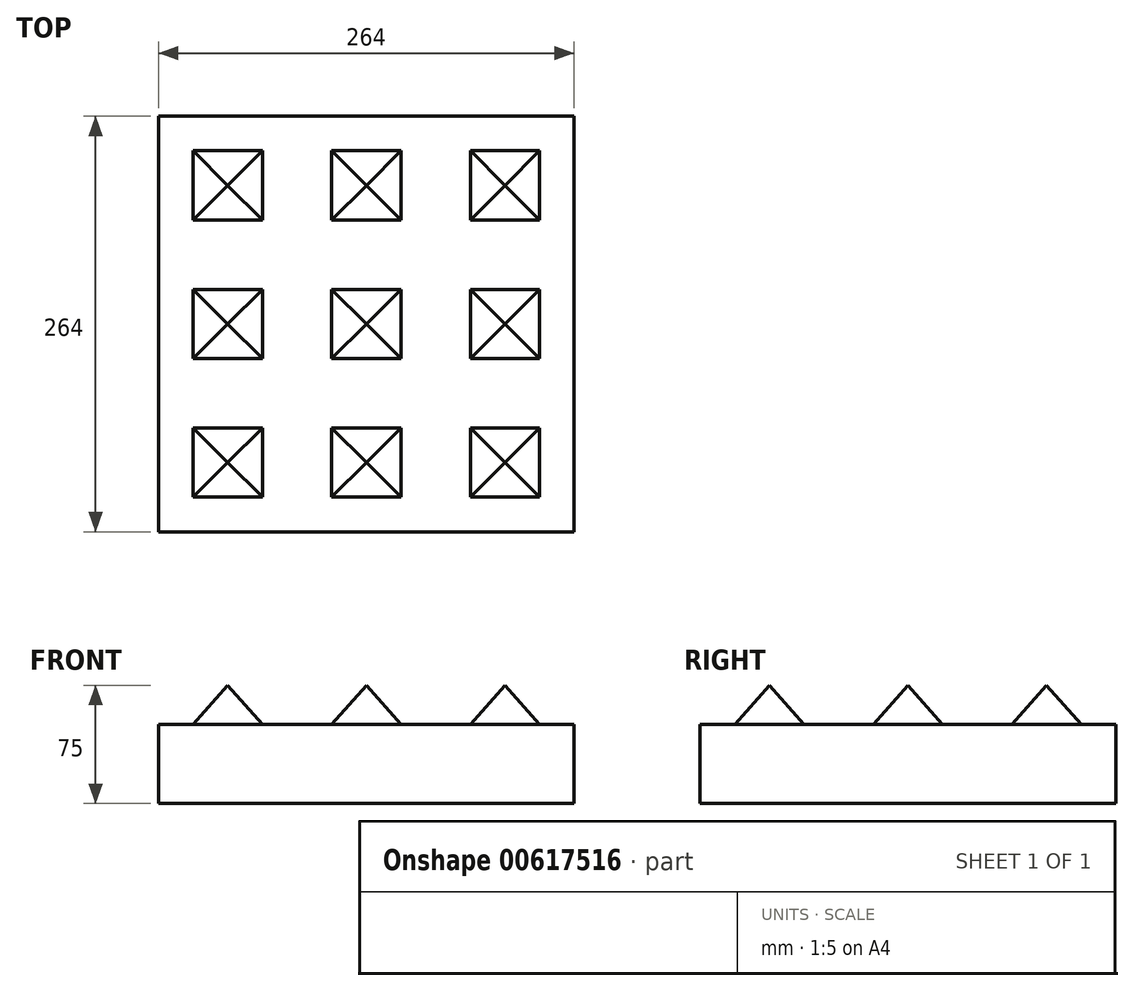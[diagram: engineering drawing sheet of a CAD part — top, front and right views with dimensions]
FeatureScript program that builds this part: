
annotation { "Feature Type Name" : "Feature", "Feature Type Description" : "" }
export const myFeature = defineFeature(function(context is Context, id is Id, definition is map)
    precondition{}
    {
        {
            var Q0;
            Q0=qCreatedBy(makeId("Top.planeOp"),FACE);
            var sketch = newSketch(context, id + "F0", { "sketchPlane" : qUnion([Q0])});
            skLineSegment(sketch, "E0.bottom", {"start": v(22, -22) * mm, "end": v(-22, -22) * mm});
            skLineSegment(sketch, "E0.top", {"start": v(22, 22) * mm, "end": v(-22, 22) * mm});
            skLineSegment(sketch, "E0.left", {"start": v(22, -22) * mm, "end": v(22, 22) * mm});
            skLineSegment(sketch, "E0.right", {"start": v(-22, -22) * mm, "end": v(-22, 22) * mm});
            skPoint(sketch, "E0.middle", {"position": v(0, 0) * mm});
            skLineSegment(sketch, "E1.bottom", {"start": v(-66, -22) * mm, "end": v(-110, -22) * mm});
            skLineSegment(sketch, "E1.top", {"start": v(-66, 22) * mm, "end": v(-110, 22) * mm});
            skLineSegment(sketch, "E1.left", {"start": v(-66, -22) * mm, "end": v(-66, 22) * mm});
            skLineSegment(sketch, "E1.right", {"start": v(-110, -22) * mm, "end": v(-110, 22) * mm});
            skPoint(sketch, "E1.middle", {"position": v(-88, 0) * mm});
            skPoint(sketch, "E1.middle.positionSnap0", {"position": v(-22, 0) * mm});
            skPoint(sketch, "E1.centerSnap0", {"position": v(-22, 0) * mm});
            skLineSegment(sketch, "E2.bottom", {"start": v(22, 66) * mm, "end": v(-22, 66) * mm});
            skLineSegment(sketch, "E2.top", {"start": v(22, 110) * mm, "end": v(-22, 110) * mm});
            skLineSegment(sketch, "E2.left", {"start": v(22, 66) * mm, "end": v(22, 110) * mm});
            skLineSegment(sketch, "E2.right", {"start": v(-22, 66) * mm, "end": v(-22, 110) * mm});
            skLineSegment(sketch, "E3.bottom", {"start": v(-66, 66) * mm, "end": v(-110, 66) * mm});
            skLineSegment(sketch, "E3.top", {"start": v(-66, 110) * mm, "end": v(-110, 110) * mm});
            skLineSegment(sketch, "E3.left", {"start": v(-66, 66) * mm, "end": v(-66, 110) * mm});
            skLineSegment(sketch, "E3.right", {"start": v(-110, 66) * mm, "end": v(-110, 110) * mm});
            skLineSegment(sketch, "E4.bottom", {"start": v(-132, 132) * mm, "end": v(132, 132) * mm});
            skLineSegment(sketch, "E4.top", {"start": v(-132, -132) * mm, "end": v(132, -132) * mm});
            skLineSegment(sketch, "E4.left", {"start": v(-132, 132) * mm, "end": v(-132, -132) * mm});
            skLineSegment(sketch, "E4.right", {"start": v(132, 132) * mm, "end": v(132, -132) * mm});
            skSolve(sketch);
        }
        {
            var Q0;
            Q0=makeQuery(id+"F0.imprint","IMPRINT",FACE,{"disambiguationData":[TD([[makeQuery(id+"F0.imprint","IMPRINT",EDGE,{"derivedFrom":sQuery(id+"F0.wireOp",EDGE,"E1.bottom")}),-1.0]])]});
            var Q1;
            Q1=makeQuery(id+"F0.imprint","IMPRINT",FACE,{"disambiguationData":[TD([[makeQuery(id+"F0.imprint","IMPRINT",EDGE,{"derivedFrom":sQuery(id+"F0.wireOp",EDGE,"E3.bottom")}),-1.0]])]});
            var Q2;
            Q2=makeQuery(id+"F0.imprint","IMPRINT",FACE,{"disambiguationData":[TD([[makeQuery(id+"F0.imprint","IMPRINT",EDGE,{"derivedFrom":sQuery(id+"F0.wireOp",EDGE,"E2.bottom")}),-1.0]])]});
            var Q3;
            Q3=makeQuery(id+"F0.imprint","IMPRINT",FACE,{"disambiguationData":[TD([[makeQuery(id+"F0.imprint","IMPRINT",EDGE,{"derivedFrom":sQuery(id+"F0.wireOp",EDGE,"E0.bottom")}),-1.0]])]});
            extrude(context, id + "F1", {"entities" : qUnion([Q0, Q1, Q2, Q3]), "depth" : 25 * mm, "offsetDistance" : 25 * mm, "hasDraft" : true, "draftAngle" : 41.35 * degree, "draftPullDirection" : true});
        }
        {
            var Q0;
            Q0=makeQuery(id+"F1.opExtrude","SWEPT_BODY",BODY,{"disambiguationData":[OSD([sQuery(id+"F0.wireOp",EDGE,"E1.bottom"),sQuery(id+"F0.wireOp",EDGE,"E1.top"),sQuery(id+"F0.wireOp",EDGE,"E1.left"),sQuery(id+"F0.wireOp",EDGE,"E1.right")])]});
            var Q1;
            Q1=makeQuery(id+"F1.opExtrude","SWEPT_BODY",BODY,{"disambiguationData":[OSD([sQuery(id+"F0.wireOp",EDGE,"E3.bottom"),sQuery(id+"F0.wireOp",EDGE,"E3.top"),sQuery(id+"F0.wireOp",EDGE,"E3.left"),sQuery(id+"F0.wireOp",EDGE,"E3.right")])]});
            var Q2;
            Q2=qCreatedBy(makeId("Right.planeOp"),FACE);
            mirror(context, id + "F2", {"entities" : qUnion([Q0, Q1]), "mirrorPlane" : qUnion([Q2])});
        }
        {
            var Q0;
            Q0=makeQuery(id+"F1.opExtrude","SWEPT_BODY",BODY,{"disambiguationData":[OSD([sQuery(id+"F0.wireOp",EDGE,"E3.bottom"),sQuery(id+"F0.wireOp",EDGE,"E3.top"),sQuery(id+"F0.wireOp",EDGE,"E3.left"),sQuery(id+"F0.wireOp",EDGE,"E3.right")])]});
            var Q1;
            Q1=makeQuery(id+"F1.opExtrude","SWEPT_BODY",BODY,{"disambiguationData":[OSD([sQuery(id+"F0.wireOp",EDGE,"E2.bottom"),sQuery(id+"F0.wireOp",EDGE,"E2.top"),sQuery(id+"F0.wireOp",EDGE,"E2.left"),sQuery(id+"F0.wireOp",EDGE,"E2.right")])]});
            var Q2;
            Q2=makeQuery(id+"F2.opPattern","COPY",BODY,{"derivedFrom":makeQuery(id+"F1.opExtrude","SWEPT_BODY",BODY,{"disambiguationData":[OSD([sQuery(id+"F0.wireOp",EDGE,"E3.bottom"),sQuery(id+"F0.wireOp",EDGE,"E3.top"),sQuery(id+"F0.wireOp",EDGE,"E3.left"),sQuery(id+"F0.wireOp",EDGE,"E3.right")])]}),"instanceName":"1"});
            var Q3;
            Q3=qCreatedBy(makeId("Front.planeOp"),FACE);
            mirror(context, id + "F3", {"entities" : qUnion([Q0, Q1, Q2]), "mirrorPlane" : qUnion([Q3])});
        }
        {
            var Q0;
            Q0=makeQuery(id+"F0.imprint","IMPRINT",FACE,{"disambiguationData":[TD([[makeQuery(id+"F0.imprint","IMPRINT",EDGE,{"derivedFrom":sQuery(id+"F0.wireOp",EDGE,"E0.bottom")}),1.0]])]});
            var Q1;
            Q1=makeQuery(id+"F0.imprint","IMPRINT",FACE,{"disambiguationData":[TD([[makeQuery(id+"F0.imprint","IMPRINT",EDGE,{"derivedFrom":sQuery(id+"F0.wireOp",EDGE,"E1.bottom")}),-1.0]])]});
            var Q2;
            Q2=makeQuery(id+"F0.imprint","IMPRINT",FACE,{"disambiguationData":[TD([[makeQuery(id+"F0.imprint","IMPRINT",EDGE,{"derivedFrom":sQuery(id+"F0.wireOp",EDGE,"E0.bottom")}),-1.0]])]});
            var Q3;
            Q3=makeQuery(id+"F0.imprint","IMPRINT",FACE,{"disambiguationData":[TD([[makeQuery(id+"F0.imprint","IMPRINT",EDGE,{"derivedFrom":sQuery(id+"F0.wireOp",EDGE,"E3.bottom")}),-1.0]])]});
            var Q4;
            Q4=makeQuery(id+"F0.imprint","IMPRINT",FACE,{"disambiguationData":[TD([[makeQuery(id+"F0.imprint","IMPRINT",EDGE,{"derivedFrom":sQuery(id+"F0.wireOp",EDGE,"E2.bottom")}),-1.0]])]});
            extrude(context, id + "F4", {"entities" : qUnion([Q0, Q1, Q2, Q3, Q4]), "oppositeDirection" : true, "depth" : 50 * mm, "offsetDistance" : 25 * mm});
        }
    });
